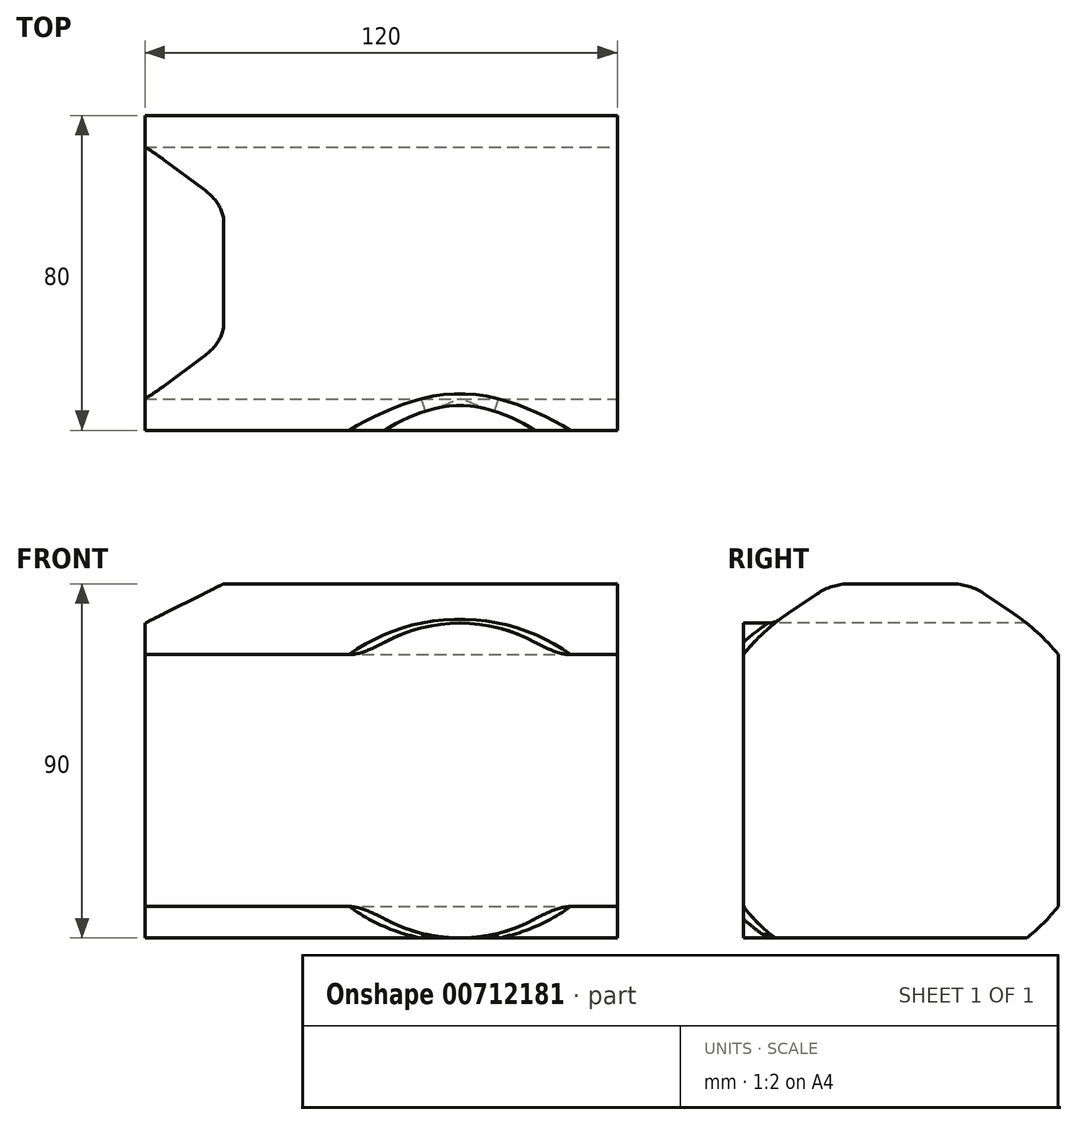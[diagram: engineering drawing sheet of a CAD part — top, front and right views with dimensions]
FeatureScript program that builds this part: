
annotation { "Feature Type Name" : "Feature", "Feature Type Description" : "" }
export const myFeature = defineFeature(function(context is Context, id is Id, definition is map)
    precondition{}
    {
        {
            var Q0;
            Q0=qCreatedBy(makeId("Right.planeOp"),FACE);
            var sketch = newSketch(context, id + "F0", { "sketchPlane" : qUnion([Q0])});
            skLineSegment(sketch, "E0.bottom", {"start": v(-40, 40) * mm, "end": v(40, 40) * mm, "construction": true});
            skLineSegment(sketch, "E0.top", {"start": v(-40, -40) * mm, "end": v(40, -40) * mm});
            skLineSegment(sketch, "E0.left", {"start": v(-40, 40) * mm, "end": v(-40, -40) * mm});
            skLineSegment(sketch, "E0.right", {"start": v(40, 40) * mm, "end": v(40, -40) * mm});
            skPoint(sketch, "E0.middle", {"position": v(0, 0) * mm});
            skLineSegment(sketch, "E1", {"start": v(-40, 40) * mm, "end": v(-40, 70) * mm});
            skLineSegment(sketch, "E2", {"start": v(-40, 70) * mm, "end": v(40, 70) * mm});
            skLineSegment(sketch, "E3", {"start": v(40, 70) * mm, "end": v(40, 40) * mm});
            skSolve(sketch);
        }
        {
            var Q0;
            Q0 = qSketchRegion(id + "F0", true);
            extrude(context, id + "F1", {"entities" : qUnion([Q0]), "depth" : 120 * mm, "offsetDistance" : 25 * mm});
        }
        {
            var Q0;
            Q0=makeQuery(id+"F1.opExtrude","CAP_FACE",FACE,{"disambiguationData":[OSD([sQuery(id+"F0.wireOp",EDGE,"E0.top"),sQuery(id+"F0.wireOp",EDGE,"E0.left"),sQuery(id+"F0.wireOp",EDGE,"E0.right"),sQuery(id+"F0.wireOp",EDGE,"E1"),sQuery(id+"F0.wireOp",EDGE,"E2"),sQuery(id+"F0.wireOp",EDGE,"E3")])],"isStart":false});
            var sketch = newSketch(context, id + "F2", { "sketchPlane" : qUnion([Q0])});
            skArc(sketch, "E4", {"start": v(-28.68, 42.44) * mm, "mid": v(-34.74, 37.65) * mm, "end": v(-40, 32) * mm});
            skLineSegment(sketch, "E5", {"start": v(-40, 40) * mm, "end": v(40, 40) * mm, "construction": true});
            skLineSegment(sketch, "E6", {"start": v(-40, 40) * mm, "end": v(-40, 32) * mm});
            skLineSegment(sketch, "E7", {"start": v(-28.68, 42.44) * mm, "end": v(-17.5, 50) * mm});
            skLineSegment(sketch, "E8", {"start": v(-17.5, 50) * mm, "end": v(0, 50) * mm});
            skLineSegment(sketch, "E9", {"start": v(0, 50) * mm, "end": v(0, 0) * mm, "construction": true});
            skLineSegment(sketch, "E10", {"start": v(-40, -40) * mm, "end": v(-40, -32) * mm});
            skLineSegment(sketch, "E11", {"start": v(-40, -40) * mm, "end": v(-32, -40) * mm});
            skLineSegment(sketch, "E12", {"start": v(40, -40) * mm, "end": v(40, -32) * mm});
            skLineSegment(sketch, "E13", {"start": v(40, -40) * mm, "end": v(32, -40) * mm});
            skLineSegment(sketch, "E14", {"start": v(40, 40) * mm, "end": v(40, 32) * mm});
            skLineSegment(sketch, "E15", {"start": v(0, 50) * mm, "end": v(17.5, 50) * mm});
            skLineSegment(sketch, "E16", {"start": v(17.5, 50) * mm, "end": v(28.68, 42.44) * mm});
            skLineSegment(sketch, "E17", {"start": v(-40, 40) * mm, "end": v(-40, 70) * mm});
            skLineSegment(sketch, "E18", {"start": v(-40, 70) * mm, "end": v(40, 70) * mm});
            skLineSegment(sketch, "E19", {"start": v(40, 70) * mm, "end": v(40, 40) * mm});
            skArc(sketch, "E20.trimOffspring", {"start": v(-40, -32) * mm, "mid": v(-36.22, -36.22) * mm, "end": v(-32, -40) * mm});
            skArc(sketch, "E21.trimOffspring", {"start": v(32, -40) * mm, "mid": v(36.22, -36.22) * mm, "end": v(40, -32) * mm});
            skArc(sketch, "E22.trimOffspring", {"start": v(40, 32) * mm, "mid": v(34.74, 37.65) * mm, "end": v(28.68, 42.44) * mm});
            skArc(sketch, "E23", {"start": v(-28.68, 42.44) * mm, "mid": v(0, 51.22) * mm, "end": v(28.68, 42.44) * mm, "construction": true});
            skSolve(sketch);
        }
        {
            var Q0;
            Q0 = qSketchRegion(id + "F2", true);
            extrude(context, id + "F3", {"entities" : qUnion([Q0]), "operationType" : NewBodyOperationType.REMOVE, "endBound" : BoundingType.THROUGH_ALL, "oppositeDirection" : true, "depth" : 25 * mm, "offsetDistance" : 25 * mm});
        }
        {
            var Q0;
            Q0=makeQuery(id+"F3.boolean.opBoolean","COPY",EDGE,{"derivedFrom":makeQuery(id+"F3.opExtrude","SWEPT_EDGE",EDGE,{"disambiguationData":[OSD([sQuery(id+"F2.wireOp",EDGE,"E15"),sQuery(id+"F2.wireOp",EDGE,"E16")])]})});
            var Q1;
            Q1=makeQuery(id+"F3.boolean.opBoolean","COPY",EDGE,{"derivedFrom":makeQuery(id+"F3.opExtrude","SWEPT_EDGE",EDGE,{"disambiguationData":[OSD([sQuery(id+"F2.wireOp",EDGE,"E7"),sQuery(id+"F2.wireOp",EDGE,"E8")])]})});
            fillet(context, id + "F4", {"entities" : qUnion([Q0, Q1]), "radius" : 15 * mm, "tangentPropagation" : true, "allowEdgeOverflow" : false});
        }
        {
            var Q0;
            Q0=qCreatedBy(makeId("Front.planeOp"),FACE);
            var sketch = newSketch(context, id + "F5", { "sketchPlane" : qUnion([Q0])});
            skLineSegment(sketch, "E24", {"start": v(0, 40) * mm, "end": v(79.37, 40) * mm, "construction": true});
            skLineSegment(sketch, "E25", {"start": v(0, 40) * mm, "end": v(0, 0) * mm, "construction": true});
            skLineSegment(sketch, "E26", {"start": v(0, 40) * mm, "end": v(20, 50) * mm});
            skLineSegment(sketch, "E27", {"start": v(20, 50) * mm, "end": v(0, 50) * mm});
            skLineSegment(sketch, "E28", {"start": v(0, 50) * mm, "end": v(0, 40) * mm});
            skSolve(sketch);
        }
        {
            var Q0;
            Q0 = qSketchRegion(id + "F5", true);
            extrude(context, id + "F6", {"entities" : qUnion([Q0]), "operationType" : NewBodyOperationType.REMOVE, "endBound" : BoundingType.THROUGH_ALL, "oppositeDirection" : true, "depth" : 25 * mm, "offsetDistance" : 25 * mm, "hasSecondDirection" : true, "secondDirectionBound" : BoundingType.THROUGH_ALL, "secondDirectionOppositeDirection" : false, "secondDirectionDepth" : 25 * mm});
        }
        {
            var Q0;
            Q0=makeQuery(id+"F1.opExtrude","SWEPT_FACE",FACE,{"disambiguationData":[OSD([sQuery(id+"F0.wireOp",EDGE,"E0.left"),sQuery(id+"F0.wireOp",EDGE,"E1")])]});
            var sketch = newSketch(context, id + "F7", { "sketchPlane" : qUnion([Q0])});
            skLineSegment(sketch, "E29", {"start": v(0, 0) * mm, "end": v(120, 0) * mm, "construction": true});
            skCircle(sketch, "E30", {"center": v(80, 0) * mm, "radius": 40 * mm});
            skSolve(sketch);
        }
        {
            var Q0;
            Q0 = qSketchRegion(id + "F7", true);
            var Q1;
            Q1=makeQuery(id+"F3.boolean.opBoolean","COPY",FACE,{"derivedFrom":makeQuery(id+"F3.opExtrude","SWEPT_FACE",FACE,{"disambiguationData":[OSD([sQuery(id+"F2.wireOp",EDGE,"E4")])]})});
            extrude(context, id + "F8", {"entities" : qUnion([Q0]), "operationType" : NewBodyOperationType.ADD, "oppositeDirection" : true, "depth" : 10 * mm, "endBoundEntityFace" : qUnion([Q1]), "offsetDistance" : 25 * mm});
        }
        {
            var Q0;
            Q0=makeQuery(id+"F8.boolean.opBoolean","INTERSECT",EDGE,{"derivedFrom":[makeQuery(id+"F3.boolean.opBoolean","COPY",FACE,{"derivedFrom":makeQuery(id+"F3.opExtrude","SWEPT_FACE",FACE,{"disambiguationData":[OSD([sQuery(id+"F2.wireOp",EDGE,"E4")])]})}),makeQuery(id+"F8.opExtrude","SWEPT_FACE",FACE,{"disambiguationData":[OSD([sQuery(id+"F7.wireOp",EDGE,"E30")])]})]});
            var Q1;
            Q1=makeQuery(id+"F8.boolean.opBoolean","INTERSECT",EDGE,{"disambiguationData":[OD(0.0)],"derivedFrom":[makeQuery(id+"F3.boolean.opBoolean","COPY",FACE,{"derivedFrom":makeQuery(id+"F3.opExtrude","SWEPT_FACE",FACE,{"disambiguationData":[OSD([sQuery(id+"F2.wireOp",EDGE,"E20.trimOffspring")])]})}),makeQuery(id+"F8.opExtrude","SWEPT_FACE",FACE,{"disambiguationData":[OSD([sQuery(id+"F7.wireOp",EDGE,"E30")])]})]});
            var Q2;
            Q2=makeQuery(id+"F8.boolean.opBoolean","INTERSECT",EDGE,{"disambiguationData":[OD(1.0)],"derivedFrom":[makeQuery(id+"F3.boolean.opBoolean","COPY",FACE,{"derivedFrom":makeQuery(id+"F3.opExtrude","SWEPT_FACE",FACE,{"disambiguationData":[OSD([sQuery(id+"F2.wireOp",EDGE,"E20.trimOffspring")])]})}),makeQuery(id+"F8.opExtrude","SWEPT_FACE",FACE,{"disambiguationData":[OSD([sQuery(id+"F7.wireOp",EDGE,"E30")])]})]});
            fillet(context, id + "F9", {"entities" : qUnion([Q0, Q1, Q2]), "radius" : 5 * mm, "tangentPropagation" : true, "allowEdgeOverflow" : false});
        }
    });
